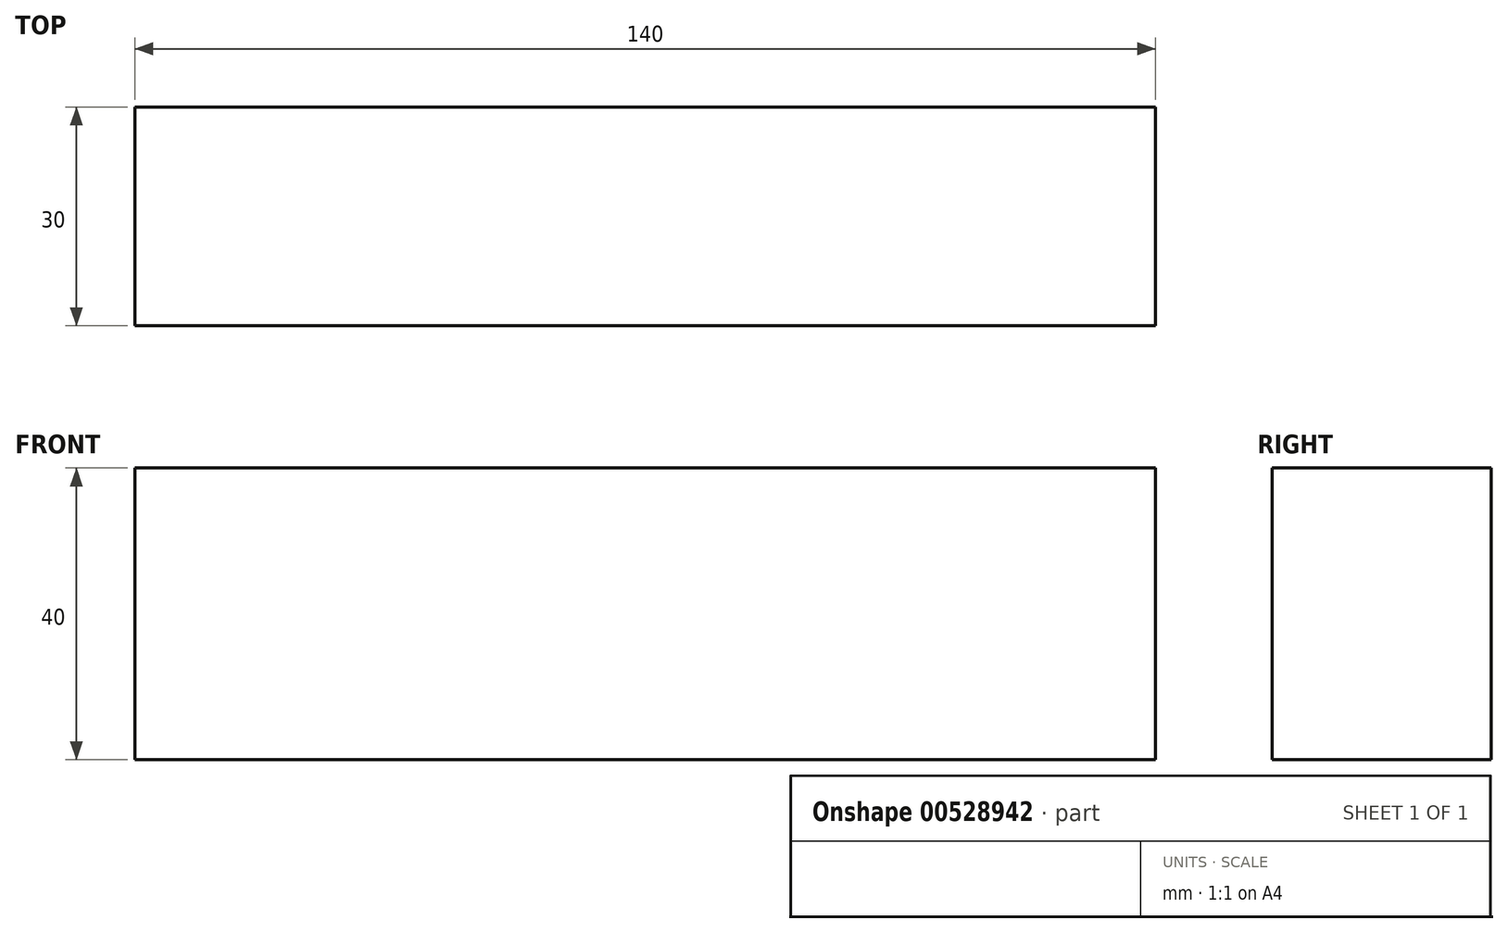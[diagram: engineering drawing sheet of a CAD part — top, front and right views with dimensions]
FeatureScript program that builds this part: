
annotation { "Feature Type Name" : "Feature", "Feature Type Description" : "" }
export const myFeature = defineFeature(function(context is Context, id is Id, definition is map)
    precondition{}
    {
        {
            var Q0;
            Q0=qCreatedBy(makeId("Top.planeOp"),FACE);
            var sketch = newSketch(context, id + "F0", { "sketchPlane" : qUnion([Q0])});
            skLineSegment(sketch, "E0.bottom", {"start": v(70, -15) * mm, "end": v(-70, -15) * mm});
            skLineSegment(sketch, "E0.top", {"start": v(70, 15) * mm, "end": v(-70, 15) * mm});
            skLineSegment(sketch, "E0.left", {"start": v(70, -15) * mm, "end": v(70, 15) * mm});
            skLineSegment(sketch, "E0.right", {"start": v(-70, -15) * mm, "end": v(-70, 15) * mm});
            skPoint(sketch, "E0.middle", {"position": v(0, 0) * mm});
            skSolve(sketch);
        }
        {
            var Q0;
            Q0=makeQuery(id+"F0.imprint","IMPRINT",FACE,{"disambiguationData":[TD([[makeQuery(id+"F0.imprint","IMPRINT",EDGE,{"derivedFrom":sQuery(id+"F0.wireOp",EDGE,"E0.bottom")}),-1.0]])]});
            extrude(context, id + "F1", {"entities" : qUnion([Q0]), "depth" : 40 * mm, "offsetDistance" : 25 * mm});
        }
    });
